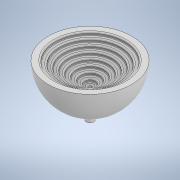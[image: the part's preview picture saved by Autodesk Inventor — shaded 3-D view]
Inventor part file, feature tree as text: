
AUTODESK INVENTOR PART (.ipt)
format: ipt  version: 2022 (Build 260153000, 153)  size: 440,832 bytes
history: native  units: mm
features: extrude x18, sketch x18, other x11, fillet x6
ambient origin geometry x8: Origin, YZ Plane, XZ Plane, XY Plane, X Axis, Y Axis, Z Axis, Center Point
bodies: Body1 (feature_tree)
feature tree (53):
  other  "實體1"
  extrude  "擠出1"  Depth=60.0mm
  fillet  "圓角1"  Radius=30.0mm
  extrude  "擠出2"  Depth=30.0mm
  extrude  "擠出3"  Depth=50.0mm
  extrude  "擠出4"  Depth=2.0mm TaperAngle=0.0deg
  extrude  "擠出5"  Depth=44.0mm
  extrude  "擠出6"  Depth=2.0mm TaperAngle=0.0deg
  extrude  "擠出7"  Depth=38.0mm
  extrude  "擠出8"  Depth=2.0mm TaperAngle=0.0deg
  extrude  "擠出9"  Depth=32.0mm
  extrude  "擠出11"  Depth=2.0mm TaperAngle=0.0deg
  extrude  "擠出12"  Depth=26.0mm
  extrude  "擠出13"  Depth=2.0mm TaperAngle=0.0deg
  extrude  "擠出16"  Depth=20.0mm
  fillet  "圓角2"  Radius=2.0mm
  extrude  "擠出17"  Depth=14.0mm
  fillet  "圓角3"  Radius=2.0mm
  extrude  "擠出18"  Depth=8.0mm
  fillet  "圓角4"  Radius=2.0mm
  extrude  "擠出19"  Depth=3.0mm
  fillet  "圓角5"  Radius=2.0mm
  other  "面圓角1"
  other  "面圓角2"
  other  "面圓角3"
  other  "面圓角4"
  other  "面圓角5"
  other  "面圓角6"
  other  "面圓角7"
  other  "面圓角8"
  extrude  "擠出20"  Depth=3.0mm
  other  "面圓角9"
  fillet  "圓角6"  Radius=50.0mm
  extrude  "擠出21"  Depth=3.0mm
  other  "面圓角10"
  sketch  "草圖3"
  sketch  "草圖4"
  sketch  "草圖5"
  sketch  "草圖6"
  sketch  "草圖7"
  sketch  "草圖8"
  sketch  "草圖9"
  sketch  "草圖10"
  sketch  "草圖11"
  sketch  "草圖14"
  sketch  "草圖15"
  sketch  "草圖16"
  sketch  "草圖25"
  sketch  "草圖26"
  sketch  "草圖27"
  sketch  "草圖29"
  sketch  "草圖30"
  sketch  "草圖31"
